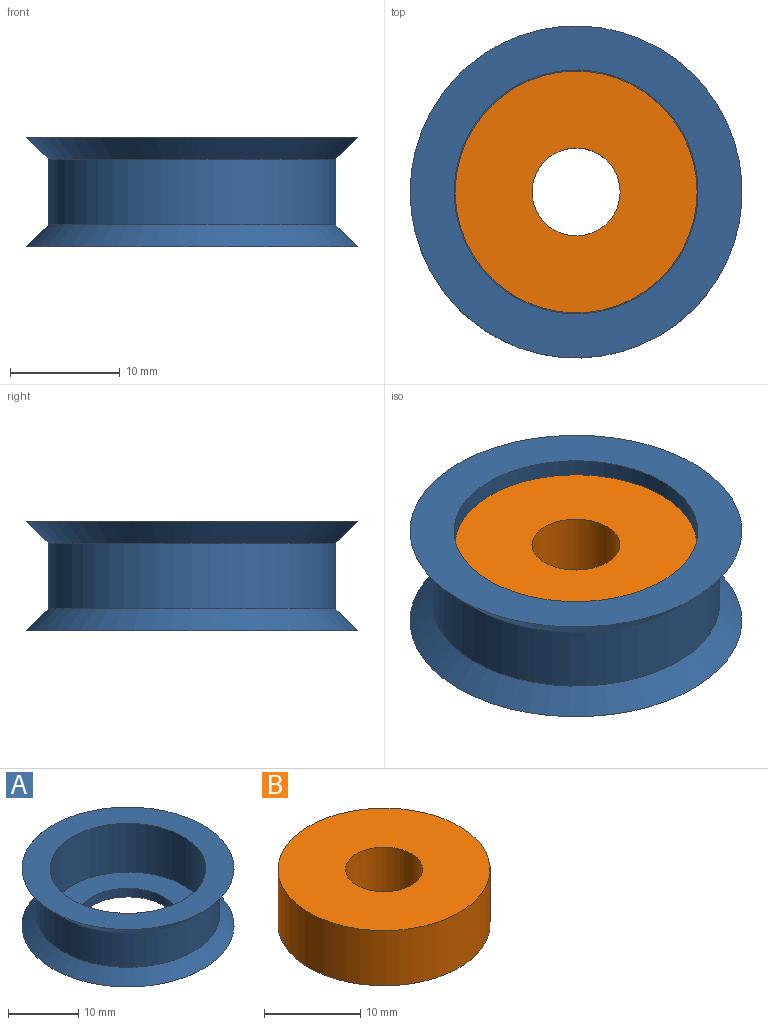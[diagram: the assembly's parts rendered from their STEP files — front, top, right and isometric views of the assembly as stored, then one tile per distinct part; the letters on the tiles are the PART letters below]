
ASSEMBLY  parts=2 mates=1
PART A: 8 faces, bbox 30.2x30.2x10 mm
  f0: plane 30.2x30.2mm, normal (0,0,1), area 329.2mm2, adj f1,f7
  f1: cylinder r=11.1mm len=22.2mm, axis (0,0,-1), area 592.8mm2, adj f0,f2
  f2: plane 22.2x22.2mm, normal (0,0,1), area 228.7mm2, adj f1,f3
  f3: cylinder r=7.1mm len=14.2mm, axis (0,0,-1), area 66.9mm2, adj f2,f4
  f4: plane 30.2x30.2mm, normal (0,0,-1), area 557.9mm2, adj f3,f5
  f5: cone r=13.1mm half-angle=45deg, axis (0,0,-1), area 250.6mm2, adj f4,f6
  f6: cylinder r=13.1mm len=26.2mm, axis (0,0,-1), area 493.9mm2, adj f5,f7
  f7: cone r=15.1mm half-angle=45deg, axis (0,0,1), area 250.6mm2, adj f0,f6
PART B: 4 faces, bbox 22x22x7 mm
  f0: cylinder r=4mm len=8mm, axis (0,0,-1), area 175.9mm2, adj f2,f3
  f1: cylinder r=11mm len=22mm, axis (0,0,-1), area 483.8mm2, adj f2,f3
  f2: plane 22x22mm, normal (0,0,1), area 329.9mm2, adj f0,f1
  f3: plane 22x22mm, normal (0,0,-1), area 329.9mm2, adj f0,f1
PLACE A t=(4.74,5.32,1.07)mm
PLACE B rot(axis=(1,0,0),180deg) t=(4.74,5.32,4.38)mm
MATE fastened B.f0 <-> A.f1  axis (0,0,1) through (4.74,5.32,-2.62)mm
